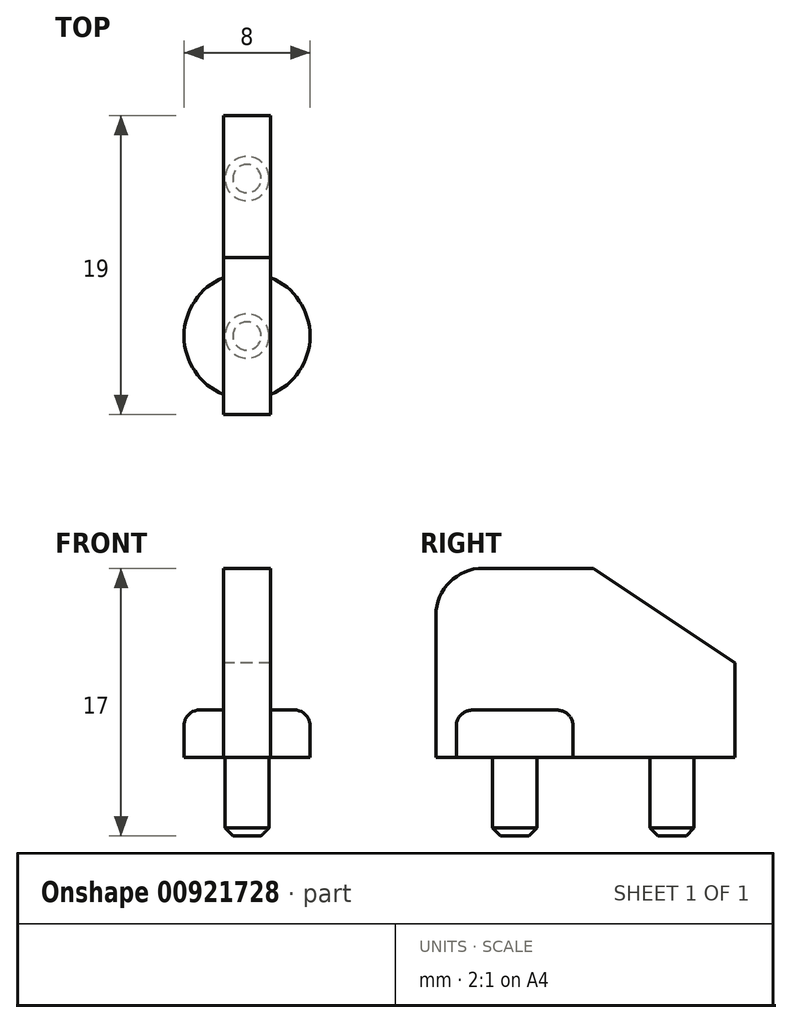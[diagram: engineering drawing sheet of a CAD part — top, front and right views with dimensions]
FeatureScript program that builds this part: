
annotation { "Feature Type Name" : "Feature", "Feature Type Description" : "" }
export const myFeature = defineFeature(function(context is Context, id is Id, definition is map)
    precondition{}
    {
        {
            var Q0;
            Q0=qCreatedBy(makeId("Top.planeOp"),FACE);
            var sketch = newSketch(context, id + "F0", { "sketchPlane" : qUnion([Q0])});
            skCircle(sketch, "E0", {"center": v(0, 5) * mm, "radius": 1.4 * mm});
            skCircle(sketch, "E1", {"center": v(0, -5) * mm, "radius": 1.4 * mm});
            skLineSegment(sketch, "E2.bottom", {"start": v(-1.5, 9) * mm, "end": v(1.5, 9) * mm});
            skLineSegment(sketch, "E2.top", {"start": v(-1.5, -10) * mm, "end": v(1.5, -10) * mm});
            skLineSegment(sketch, "E2.left", {"start": v(-1.5, 9) * mm, "end": v(-1.5, -10) * mm});
            skLineSegment(sketch, "E2.right", {"start": v(1.5, 9) * mm, "end": v(1.5, -10) * mm});
            skPoint(sketch, "E3.orphan", {"position": v(0, 9) * mm});
            skPoint(sketch, "E4.end.orphan", {"position": v(0, -10) * mm});
            skArc(sketch, "E5", {"start": v(1.5, -8.7) * mm, "mid": v(4, -5) * mm, "end": v(1.5, -1.3) * mm});
            skArc(sketch, "E6", {"start": v(1.5, 1.3) * mm, "mid": v(0, 9) * mm, "end": v(-1.5, 1.3) * mm});
            skArc(sketch, "E7.trimOffspring", {"start": v(-1.5, -1.3) * mm, "mid": v(-4, -5) * mm, "end": v(-1.5, -8.7) * mm});
            skSolve(sketch);
        }
        {
            var Q0;
            {var subQ5=sQuery(id+"F0.wireOp",EDGE,"E2.bottom");Q0=makeQuery(id+"F0.imprint","IMPRINT",FACE,{"disambiguationData":[TD([[makeQuery(id+"F0.imprint","IMPRINT",EDGE,{"derivedFrom":subQ5}),-1.0]])]});}
            var Q1;
            {var subQ0=sQuery(id+"F0.wireOp",EDGE,"E2.left");var subQ1=sQuery(id+"F0.wireOp",EDGE,"E0");var subQ2=makeQuery(id+"F0.imprint","INTERSECT",VERTEX,{"derivedFrom":[subQ1,subQ0]});Q1=makeQuery(id+"F0.imprint","IMPRINT",FACE,{"disambiguationData":[TD([[makeQuery(id+"F0.imprint","IMPRINT",EDGE,{"disambiguationData":[TD([[subQ2,-1.0]])],"derivedFrom":subQ1}),-1.0]])]});}
            var Q2;
            {var subQ5=sQuery(id+"F0.wireOp",EDGE,"E2.top");Q2=makeQuery(id+"F0.imprint","IMPRINT",FACE,{"disambiguationData":[TD([[makeQuery(id+"F0.imprint","IMPRINT",EDGE,{"derivedFrom":subQ5}),1.0]])]});}
            var Q3;
            {var subQ0=sQuery(id+"F0.wireOp",EDGE,"E1");var subQ1=makeQuery(id+"F0.imprint","INTERSECT",VERTEX,{"derivedFrom":[subQ0,sQuery(id+"F0.wireOp",EDGE,"E2.left")]});Q3=makeQuery(id+"F0.imprint","IMPRINT",FACE,{"disambiguationData":[TD([[makeQuery(id+"F0.imprint","IMPRINT",EDGE,{"disambiguationData":[TD([[subQ1,1.0]])],"derivedFrom":subQ0}),1.0]])]});}
            var Q4;
            {var subQ0=sQuery(id+"F0.wireOp",EDGE,"E0");var subQ1=makeQuery(id+"F0.imprint","INTERSECT",VERTEX,{"derivedFrom":[subQ0,sQuery(id+"F0.wireOp",EDGE,"E2.left")]});Q4=makeQuery(id+"F0.imprint","IMPRINT",FACE,{"disambiguationData":[TD([[makeQuery(id+"F0.imprint","IMPRINT",EDGE,{"disambiguationData":[TD([[subQ1,1.0]])],"derivedFrom":subQ0}),1.0]])]});}
            extrude(context, id + "F1", {"entities" : qUnion([Q0, Q1, Q2, Q3, Q4]), "depth" : 12 * mm, "offsetDistance" : 25 * mm});
        }
        {
            var Q0;
            {var subQ0=sQuery(id+"F0.wireOp",EDGE,"E0");var subQ1=makeQuery(id+"F0.imprint","INTERSECT",VERTEX,{"derivedFrom":[subQ0,sQuery(id+"F0.wireOp",EDGE,"E2.left")]});Q0=makeQuery(id+"F0.imprint","IMPRINT",FACE,{"disambiguationData":[TD([[makeQuery(id+"F0.imprint","IMPRINT",EDGE,{"disambiguationData":[TD([[subQ1,1.0]])],"derivedFrom":subQ0}),1.0]])]});}
            var Q1;
            {var subQ0=sQuery(id+"F0.wireOp",EDGE,"E1");var subQ1=makeQuery(id+"F0.imprint","INTERSECT",VERTEX,{"derivedFrom":[subQ0,sQuery(id+"F0.wireOp",EDGE,"E2.left")]});Q1=makeQuery(id+"F0.imprint","IMPRINT",FACE,{"disambiguationData":[TD([[makeQuery(id+"F0.imprint","IMPRINT",EDGE,{"disambiguationData":[TD([[subQ1,1.0]])],"derivedFrom":subQ0}),1.0]])]});}
            extrude(context, id + "F2", {"entities" : qUnion([Q0, Q1]), "operationType" : NewBodyOperationType.ADD, "oppositeDirection" : true, "depth" : 5 * mm, "offsetDistance" : 25 * mm});
        }
        {
            var Q0;
            Q0=makeQuery(id+"F2.opExtrude","CAP_EDGE",EDGE,{"disambiguationData":[OSD([sQuery(id+"F0.wireOp",EDGE,"E1")])],"isStart":false});
            var Q1;
            Q1=makeQuery(id+"F2.opExtrude","CAP_EDGE",EDGE,{"disambiguationData":[OSD([sQuery(id+"F0.wireOp",EDGE,"E0")])],"isStart":false});
            chamfer(context, id + "F3", {"entities" : qUnion([Q0, Q1]), "width" : 0.5 * mm, "tangentPropagation" : true});
        }
        {
            var Q0;
            {var subQ0=sQuery(id+"F0.wireOp",EDGE,"E7.trimOffspring");Q0=makeQuery(id+"F0.imprint","IMPRINT",FACE,{"disambiguationData":[TD([[makeQuery(id+"F0.imprint","IMPRINT",EDGE,{"derivedFrom":subQ0}),1.0]])]});}
            var Q1;
            {var subQ0=sQuery(id+"F0.wireOp",EDGE,"E6");var subQ1=sQuery(id+"F0.wireOp",EDGE,"E2.left");var subQ2=makeQuery(id+"F0.imprint","INTERSECT",VERTEX,{"disambiguationData":[OD(0.0)],"derivedFrom":[subQ1,subQ0]});Q1=makeQuery(id+"F0.imprint","IMPRINT",FACE,{"disambiguationData":[TD([[makeQuery(id+"F0.imprint","IMPRINT",EDGE,{"disambiguationData":[TD([[subQ2,1.0]])],"derivedFrom":subQ1}),-1.0]])]});}
            var Q2;
            {var subQ0=sQuery(id+"F0.wireOp",EDGE,"E5");Q2=makeQuery(id+"F0.imprint","IMPRINT",FACE,{"disambiguationData":[TD([[makeQuery(id+"F0.imprint","IMPRINT",EDGE,{"derivedFrom":subQ0}),1.0]])]});}
            var Q3;
            {var subQ0=sQuery(id+"F0.wireOp",EDGE,"E6");var subQ1=sQuery(id+"F0.wireOp",EDGE,"E2.right");var subQ2=makeQuery(id+"F0.imprint","INTERSECT",VERTEX,{"disambiguationData":[OD(0.0)],"derivedFrom":[subQ1,subQ0]});Q3=makeQuery(id+"F0.imprint","IMPRINT",FACE,{"disambiguationData":[TD([[makeQuery(id+"F0.imprint","IMPRINT",EDGE,{"disambiguationData":[TD([[subQ2,1.0]])],"derivedFrom":subQ1}),1.0]])]});}
            extrude(context, id + "F4", {"entities" : qUnion([Q0, Q1, Q2, Q3]), "operationType" : NewBodyOperationType.ADD, "depth" : 3 * mm, "offsetDistance" : 25 * mm});
        }
        {
            var Q0;
            {var subQ0=sQuery(id+"F0.wireOp",EDGE,"E6");var subQ1=sQuery(id+"F0.wireOp",EDGE,"E2.left");Q0=makeQuery(id+"F4.opExtrude","CAP_EDGE",EDGE,{"disambiguationData":[OSD([subQ0]),TDD([makeQuery(id+"F0.imprint","IMPRINT",EDGE,{"disambiguationData":[TD([[makeQuery(id+"F0.imprint","INTERSECT",VERTEX,{"disambiguationData":[OD(0.0)],"derivedFrom":[subQ1,subQ0]}),1.0]])],"derivedFrom":subQ0})])],"isStart":false});}
            var Q1;
            Q1=makeQuery(id+"F4.opExtrude","CAP_EDGE",EDGE,{"disambiguationData":[OSD([sQuery(id+"F0.wireOp",EDGE,"E7.trimOffspring")])],"isStart":false});
            var Q2;
            Q2=makeQuery(id+"F4.opExtrude","CAP_EDGE",EDGE,{"disambiguationData":[OSD([sQuery(id+"F0.wireOp",EDGE,"E5")])],"isStart":false});
            var Q3;
            {var subQ0=sQuery(id+"F0.wireOp",EDGE,"E6");var subQ1=sQuery(id+"F0.wireOp",EDGE,"E2.right");Q3=makeQuery(id+"F4.opExtrude","CAP_EDGE",EDGE,{"disambiguationData":[OSD([subQ0]),TDD([makeQuery(id+"F0.imprint","IMPRINT",EDGE,{"disambiguationData":[TD([[makeQuery(id+"F0.imprint","INTERSECT",VERTEX,{"disambiguationData":[OD(0.0)],"derivedFrom":[subQ1,subQ0]}),-1.0]])],"derivedFrom":subQ0})])],"isStart":false});}
            fillet(context, id + "F5", {"entities" : qUnion([Q0, Q1, Q2, Q3]), "radius" : 1 * mm, "tangentPropagation" : true, "allowEdgeOverflow" : false});
        }
        {
            var Q0;
            Q0=makeQuery(id+"F1.opExtrude","SWEPT_FACE",FACE,{"disambiguationData":[OSD([sQuery(id+"F0.wireOp",EDGE,"E2.left")])]});
            var sketch = newSketch(context, id + "F6", { "sketchPlane" : qUnion([Q0])});
            skLineSegment(sketch, "E8", {"start": v(-9, 12) * mm, "end": v(-9, 6) * mm});
            skLineSegment(sketch, "E9", {"start": v(0, 12) * mm, "end": v(-9, 6) * mm});
            skSolve(sketch);
        }
        {
            var Q0;
            Q0 = qSketchRegion(id + "F6", true);
            var Q1;
            {var subQ0=sQuery(id+"F6.wireOp",EDGE,"E8");Q1=makeQuery(id+"F6.imprint","IMPRINT",FACE,{"disambiguationData":[TD([[makeQuery(id+"F6.imprint","IMPRINT",EDGE,{"derivedFrom":subQ0}),1.0]])]});}
            extrude(context, id + "F7", {"entities" : qUnion([Q0, Q1]), "operationType" : NewBodyOperationType.REMOVE, "oppositeDirection" : true, "depth" : 25 * mm, "offsetDistance" : 25 * mm});
        }
        {
            var Q0;
            Q0=makeQuery(id+"F1.opExtrude","CAP_EDGE",EDGE,{"disambiguationData":[OSD([sQuery(id+"F0.wireOp",EDGE,"E2.top")])],"isStart":false});
            var Q1;
            Q1=makeQuery(id+"F7.boolean.opBoolean","COPY",EDGE,{"derivedFrom":makeQuery(id+"F7.opExtrude","SWEPT_EDGE",EDGE,{"disambiguationData":[OSD([sQuery(id+"F0.wireOp",EDGE,"E2.left"),sQuery(id+"F6.wireOp",EDGE,"E9")])]})});
            var Q2;
            Q2=makeQuery(id+"F7.boolean.opBoolean","COPY",EDGE,{"derivedFrom":makeQuery(id+"F7.opExtrude","SWEPT_EDGE",EDGE,{"disambiguationData":[OSD([sQuery(id+"F0.wireOp",EDGE,"E2.bottom"),sQuery(id+"F0.wireOp",EDGE,"E2.left"),sQuery(id+"F6.wireOp",EDGE,"E8"),sQuery(id+"F6.wireOp",EDGE,"E9")])]})});
            fillet(context, id + "F8", {"entities" : qUnion([Q0, Q1, Q2]), "radius" : 3 * mm, "tangentPropagation" : true, "allowEdgeOverflow" : false});
        }
    });
